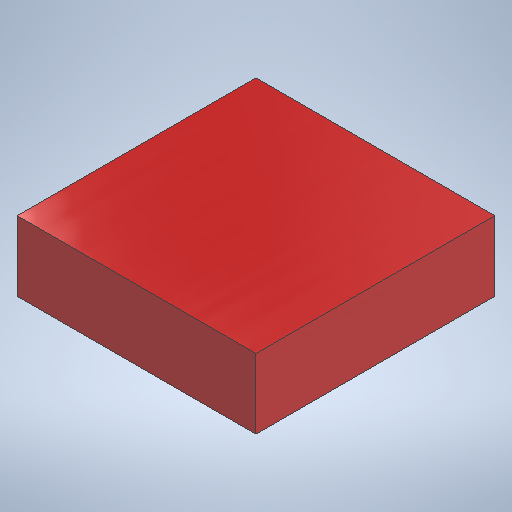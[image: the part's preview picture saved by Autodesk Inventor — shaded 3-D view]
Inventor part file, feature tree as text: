
AUTODESK INVENTOR PART (.ipt)
format: ipt  version: 2025.1 (Build 291241000, 241)  size: 214,528 bytes
history: native  units: in
note: dims shown in document units (in); Inventor stores cm internally (conversion verified against a paired STEP export)
features: extrude x1, sketch x1, other x1
ambient origin geometry x8: Origin, YZ Plane, XZ Plane, XY Plane, X Axis, Y Axis, Z Axis, Center Point
bodies: Solid1 (feature_tree)
feature tree (3):
  extrude  "Extrusion1"  Depth=5.1181in
  sketch  "Sketch1"  dims[d0=5.1181in d1=5.1181in d2=1.4961in d3=0.0in]
  other  "Finish1"
